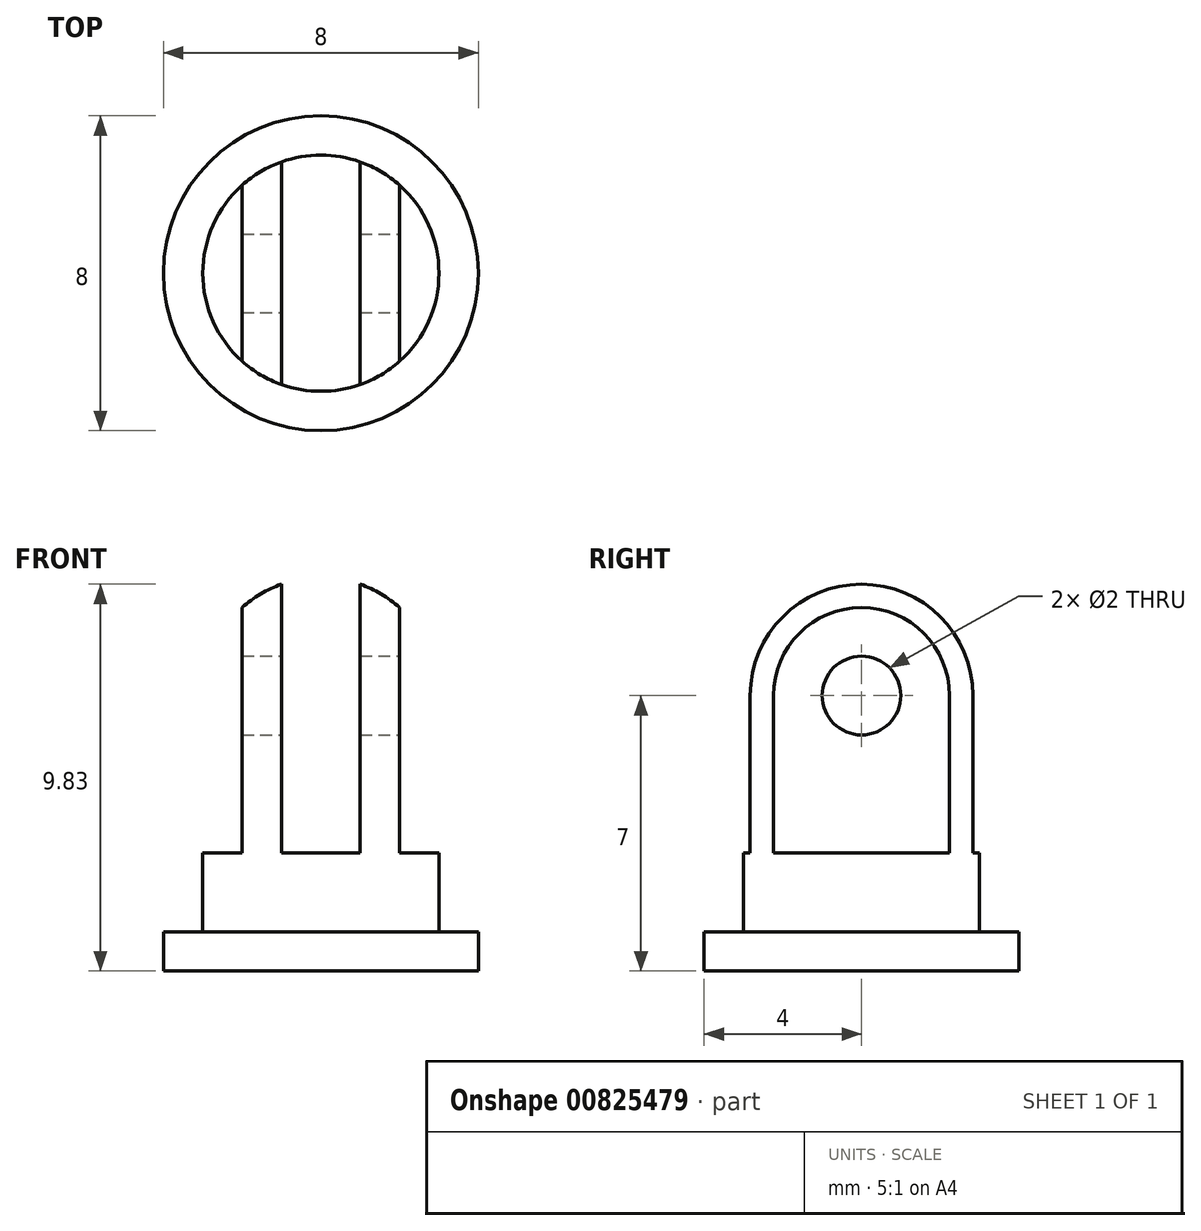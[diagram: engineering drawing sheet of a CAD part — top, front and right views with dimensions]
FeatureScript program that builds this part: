
annotation { "Feature Type Name" : "Feature", "Feature Type Description" : "" }
export const myFeature = defineFeature(function(context is Context, id is Id, definition is map)
    precondition{}
    {
        {
            var Q0;
            Q0=qCreatedBy(makeId("Top.planeOp"),FACE);
            var sketch = newSketch(context, id + "F0", { "sketchPlane" : qUnion([Q0])});
            skCircle(sketch, "E0", {"center": v(0, 0) * mm, "radius": 4 * mm});
            skSolve(sketch);
        }
        {
            var Q0;
            Q0=makeQuery(id+"F0.imprint","IMPRINT",FACE,{"disambiguationData":[TD([[makeQuery(id+"F0.imprint","IMPRINT",EDGE,{"derivedFrom":sQuery(id+"F0.wireOp",EDGE,"E0")}),1.0]])]});
            extrude(context, id + "F1", {"entities" : qUnion([Q0]), "depth" : 1 * mm, "offsetDistance" : 25 * mm});
        }
        {
            var Q0;
            Q0=makeQuery(id+"F1.opExtrude","CAP_FACE",FACE,{"disambiguationData":[OSD([sQuery(id+"F0.wireOp",EDGE,"E0")])],"isStart":false});
            var sketch = newSketch(context, id + "F2", { "sketchPlane" : qUnion([Q0])});
            skCircle(sketch, "E1", {"center": v(0, 0) * mm, "radius": 3 * mm});
            skSolve(sketch);
        }
        {
            var Q0;
            Q0=makeQuery(id+"F2.imprint","IMPRINT",FACE,{"disambiguationData":[TD([[makeQuery(id+"F2.imprint","IMPRINT",EDGE,{"derivedFrom":sQuery(id+"F2.wireOp",EDGE,"E1")}),1.0]])]});
            extrude(context, id + "F3", {"entities" : qUnion([Q0]), "operationType" : NewBodyOperationType.ADD, "depth" : 9 * mm, "offsetDistance" : 25 * mm});
        }
        {
            var Q0;
            Q0=makeQuery(id+"F3.opExtrude","CAP_EDGE",EDGE,{"disambiguationData":[OSD([sQuery(id+"F2.wireOp",EDGE,"E1")])],"isStart":false});
            fillet(context, id + "F4", {"entities" : qUnion([Q0]), "radius" : 3 * mm, "tangentPropagation" : true, "allowEdgeOverflow" : false});
        }
        {
            var Q0;
            Q0=qCreatedBy(makeId("Front.planeOp"),FACE);
            var sketch = newSketch(context, id + "F5", { "sketchPlane" : qUnion([Q0])});
            skLineSegment(sketch, "E2.bottom", {"start": v(1, 3) * mm, "end": v(-1, 3) * mm});
            skLineSegment(sketch, "E2.top", {"start": v(1, 11) * mm, "end": v(-1, 11) * mm});
            skLineSegment(sketch, "E2.left", {"start": v(1, 3) * mm, "end": v(1, 11) * mm});
            skLineSegment(sketch, "E2.right", {"start": v(-1, 3) * mm, "end": v(-1, 11) * mm});
            skPoint(sketch, "E2.middle", {"position": v(0, 7) * mm});
            skLineSegment(sketch, "E3", {"start": v(-1, 3) * mm, "end": v(-2, 3) * mm, "construction": true});
            skLineSegment(sketch, "E4", {"start": v(1, 3) * mm, "end": v(2, 3) * mm, "construction": true});
            skLineSegment(sketch, "E5.bottom", {"start": v(-2, 3) * mm, "end": v(-4, 3) * mm});
            skLineSegment(sketch, "E5.top", {"start": v(-2, 11) * mm, "end": v(-4, 11) * mm});
            skLineSegment(sketch, "E5.left", {"start": v(-2, 3) * mm, "end": v(-2, 11) * mm});
            skLineSegment(sketch, "E5.right", {"start": v(-4, 3) * mm, "end": v(-4, 11) * mm});
            skLineSegment(sketch, "E6.bottom", {"start": v(2, 3) * mm, "end": v(4, 3) * mm});
            skLineSegment(sketch, "E6.top", {"start": v(2, 11) * mm, "end": v(4, 11) * mm});
            skLineSegment(sketch, "E6.left", {"start": v(2, 3) * mm, "end": v(2, 11) * mm});
            skLineSegment(sketch, "E6.right", {"start": v(4, 3) * mm, "end": v(4, 11) * mm});
            skSolve(sketch);
        }
        {
            var Q0;
            Q0=makeQuery(id+"F5.imprint","IMPRINT",FACE,{"disambiguationData":[TD([[makeQuery(id+"F5.imprint","IMPRINT",EDGE,{"derivedFrom":sQuery(id+"F5.wireOp",EDGE,"E5.bottom")}),-1.0]])]});
            var Q1;
            Q1=makeQuery(id+"F5.imprint","IMPRINT",FACE,{"disambiguationData":[TD([[makeQuery(id+"F5.imprint","IMPRINT",EDGE,{"derivedFrom":sQuery(id+"F5.wireOp",EDGE,"E2.bottom")}),-1.0]])]});
            var Q2;
            Q2=makeQuery(id+"F5.imprint","IMPRINT",FACE,{"disambiguationData":[TD([[makeQuery(id+"F5.imprint","IMPRINT",EDGE,{"derivedFrom":sQuery(id+"F5.wireOp",EDGE,"E6.bottom")}),1.0]])]});
            extrude(context, id + "F6", {"entities" : qUnion([Q0, Q1, Q2]), "operationType" : NewBodyOperationType.REMOVE, "endBound" : BoundingType.SYMMETRIC, "depth" : 7.62 * mm, "offsetDistance" : 25 * mm});
        }
        {
            var Q0;
            Q0=makeQuery(id+"F6.boolean.opBoolean","COPY",FACE,{"derivedFrom":makeQuery(id+"F6.opExtrude","SWEPT_FACE",FACE,{"disambiguationData":[OSD([sQuery(id+"F5.wireOp",EDGE,"E6.left")])]})});
            var sketch = newSketch(context, id + "F7", { "sketchPlane" : qUnion([Q0])});
            skCircle(sketch, "E7", {"center": v(0, 7) * mm, "radius": 1 * mm});
            skSolve(sketch);
        }
        {
            var Q0;
            Q0 = qSketchRegion(id + "F7", true);
            extrude(context, id + "F8", {"entities" : qUnion([Q0]), "operationType" : NewBodyOperationType.REMOVE, "oppositeDirection" : true, "depth" : 25 * mm, "offsetDistance" : 25 * mm});
        }
    });
